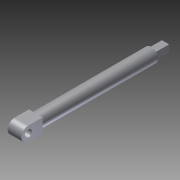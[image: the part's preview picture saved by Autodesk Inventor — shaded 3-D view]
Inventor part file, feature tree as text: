
AUTODESK INVENTOR PART (.ipt)
format: ipt  version: 2011 (Build 150239000, 239)  size: 113,664 bytes
history: native  units: in
note: dims shown in document units (in); Inventor stores cm internally (conversion verified against a paired STEP export)
features: extrude x6, sketch x6
ambient origin geometry x8: Origin, YZ Plane, XZ Plane, XY Plane, X Axis, Y Axis, Z Axis, Center Point
bodies: Solid1 (feature_tree)
feature tree (12):
  extrude  "Extrusion1"  Depth=0.5in TaperAngle=0.0deg
  extrude  "Extrusion2"  Depth=0.5in TaperAngle=0.0deg
  extrude  "Extrusion3"  Depth=0.5in TaperAngle=0.0deg
  extrude  "Extrusion4"  Depth=0.125in
  extrude  "Extrusion5"  Depth=0.25in
  extrude  "Extrusion6"  [1 undecoded]
  sketch  "Sketch1"  dims[d0=4.0in d1=0.0in d2=0.5in d3=0.0in]
  sketch  "Sketch2"  dims[d4=0.25in d5=0.5in d6=0.0in]
  sketch  "Sketch3"  dims[d7=0.5in d8=0.0in d9=0.5in d10=0.0in]
  sketch  "Sketch4"  dims[d11=0.125in d12=0.125in]
  sketch  "Sketch5"  dims[d13=0.25in d14=0.25in]
  sketch  "Sketch6"  dims[d15=0.5in d16=0.0in]
note: 1 required parameter value undecoded (feature->parameter linkage not recoverable at this tier; creation-order binding heuristic only, values carry confidence <= 0.55)
